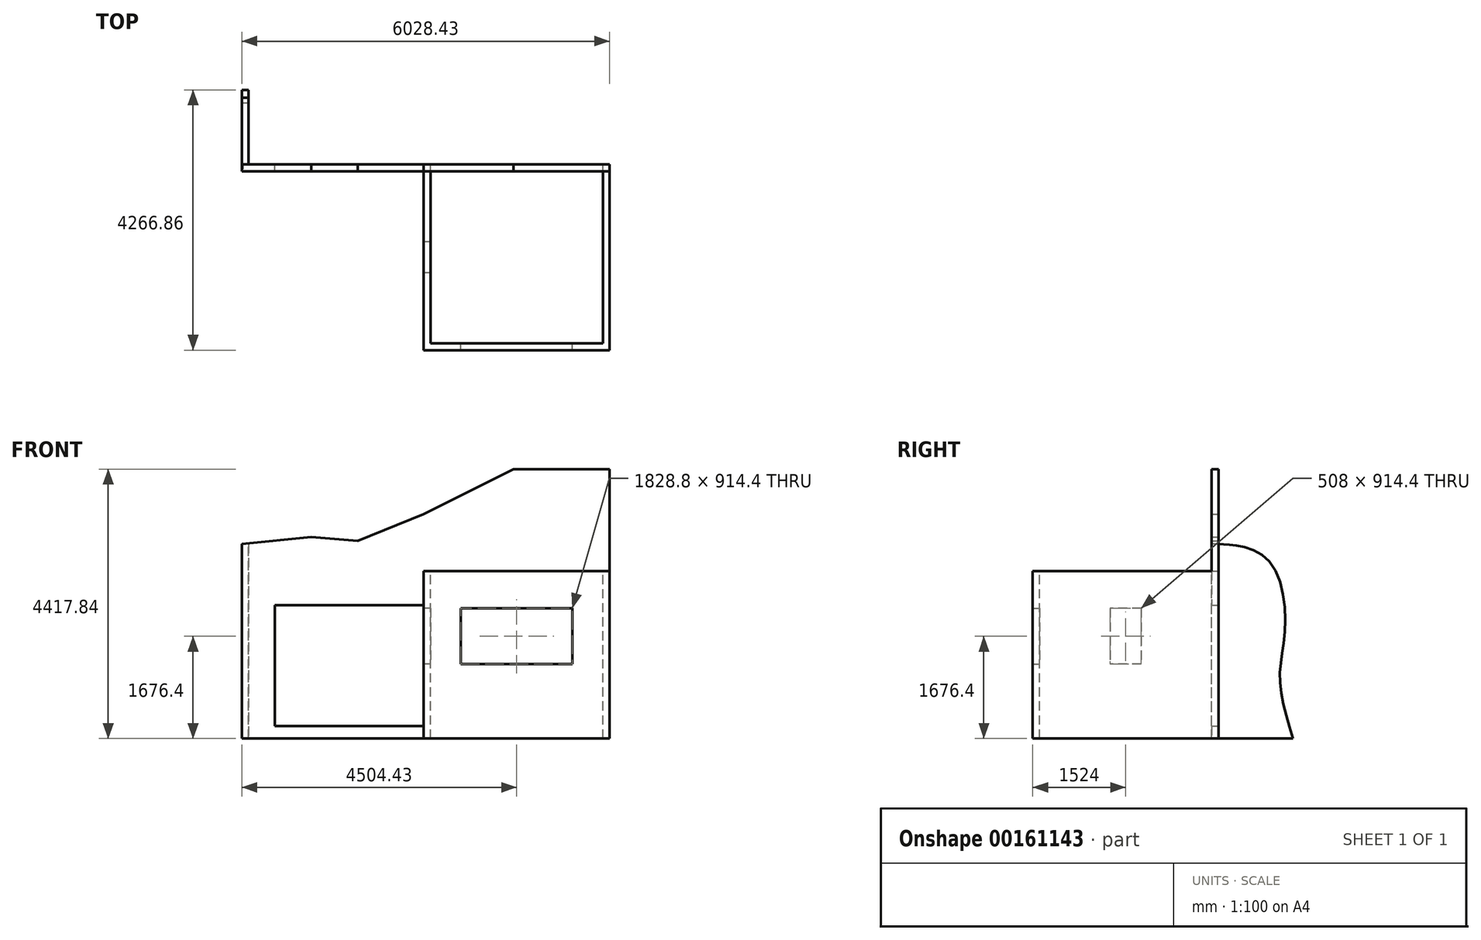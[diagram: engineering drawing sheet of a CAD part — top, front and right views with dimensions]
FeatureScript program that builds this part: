
annotation { "Feature Type Name" : "Feature", "Feature Type Description" : "" }
export const myFeature = defineFeature(function(context is Context, id is Id, definition is map)
    precondition{}
    {
        {
            var Q0;
            Q0=qCreatedBy(makeId("Front.planeOp"),FACE);
            var sketch = newSketch(context, id + "F0", { "sketchPlane" : qUnion([Q0])});
            skLineSegment(sketch, "E0.bottom", {"start": v(0, 0) * mm, "end": v(3048, 0) * mm});
            skLineSegment(sketch, "E0.top", {"start": v(0, 2743.2) * mm, "end": v(3048, 2743.2) * mm});
            skLineSegment(sketch, "E0.left", {"start": v(0, 0) * mm, "end": v(0, 2743.2) * mm});
            skLineSegment(sketch, "E0.right", {"start": v(3048, 0) * mm, "end": v(3048, 2743.2) * mm});
            skLineSegment(sketch, "E1.bottom", {"start": v(609.6, 2133.6) * mm, "end": v(2438.4, 2133.6) * mm});
            skLineSegment(sketch, "E1.top", {"start": v(609.6, 1219.2) * mm, "end": v(2438.4, 1219.2) * mm});
            skLineSegment(sketch, "E1.left", {"start": v(609.6, 2133.6) * mm, "end": v(609.6, 1219.2) * mm});
            skLineSegment(sketch, "E1.right", {"start": v(2438.4, 2133.6) * mm, "end": v(2438.4, 1219.2) * mm});
            skSolve(sketch);
        }
        {
            var Q0;
            Q0=qSketchRegion(id+"F0",true);
            extrude(context, id + "F1", {"entities" : qUnion([Q0]), "depth" : 114.04 * mm});
        }
        {
            var Q0;
            Q0=makeQuery(id+"F1.opExtrude","SWEPT_FACE",FACE,{"disambiguationData":[OSD([sQuery(id+"F0.wireOp",EDGE,"E0.left")])]});
            var sketch = newSketch(context, id + "F2", { "sketchPlane" : qUnion([Q0])});
            skLineSegment(sketch, "E2.bottom", {"start": v(114.04, 0) * mm, "end": v(-2933.96, 0) * mm});
            skLineSegment(sketch, "E2.top", {"start": v(114.04, 2743.2) * mm, "end": v(-2933.96, 2743.2) * mm});
            skLineSegment(sketch, "E2.left", {"start": v(114.04, 0) * mm, "end": v(114.04, 2743.2) * mm});
            skLineSegment(sketch, "E2.right", {"start": v(-2933.96, 0) * mm, "end": v(-2933.96, 2743.2) * mm});
            skLineSegment(sketch, "E3.bottom", {"start": v(-1663.96, 2133.6) * mm, "end": v(-1155.96, 2133.6) * mm});
            skLineSegment(sketch, "E3.top", {"start": v(-1663.96, 1219.2) * mm, "end": v(-1155.96, 1219.2) * mm});
            skLineSegment(sketch, "E3.left", {"start": v(-1663.96, 2133.6) * mm, "end": v(-1663.96, 1219.2) * mm});
            skLineSegment(sketch, "E3.right", {"start": v(-1155.96, 2133.6) * mm, "end": v(-1155.96, 1219.2) * mm});
            skSolve(sketch);
        }
        {
            var Q0;
            Q0=qSketchRegion(id+"F2",true);
            extrude(context, id + "F3", {"entities" : qUnion([Q0]), "operationType" : NewBodyOperationType.ADD, "oppositeDirection" : true, "depth" : 110 * mm});
        }
        {
            var Q0;
            Q0=makeQuery(id+"F1.opExtrude","SWEPT_FACE",FACE,{"disambiguationData":[OSD([sQuery(id+"F0.wireOp",EDGE,"E0.right")])]});
            var sketch = newSketch(context, id + "F4", { "sketchPlane" : qUnion([Q0])});
            skLineSegment(sketch, "E4.bottom", {"start": v(-114.04, 0) * mm, "end": v(2933.96, 0) * mm});
            skLineSegment(sketch, "E4.top", {"start": v(-114.04, 2743.2) * mm, "end": v(2933.96, 2743.2) * mm});
            skLineSegment(sketch, "E4.left", {"start": v(-114.04, 0) * mm, "end": v(-114.04, 2743.2) * mm});
            skLineSegment(sketch, "E4.right", {"start": v(2933.96, 0) * mm, "end": v(2933.96, 2743.2) * mm});
            skSolve(sketch);
        }
        {
            var Q0;
            Q0=qSketchRegion(id+"F4",true);
            extrude(context, id + "F5", {"entities" : qUnion([Q0]), "operationType" : NewBodyOperationType.ADD, "oppositeDirection" : true, "depth" : 110 * mm});
        }
        {
            var Q0;
            Q0=makeQuery(id+"F5.opExtrude","SWEPT_FACE",FACE,{"disambiguationData":[OSD([sQuery(id+"F4.wireOp",EDGE,"E4.right")])]});
            var sketch = newSketch(context, id + "F6", { "sketchPlane" : qUnion([Q0])});
            skLineSegment(sketch, "E5", {"start": v(-3048, 2743.2) * mm, "end": v(-67.57, 2743.2) * mm});
            skLineSegment(sketch, "E6", {"start": v(-67.57, 2743.2) * mm, "end": v(-67.57, 0) * mm});
            skLineSegment(sketch, "E7", {"start": v(-67.57, 0) * mm, "end": v(2980.43, 0) * mm});
            skLineSegment(sketch, "E8", {"start": v(2980.43, 0) * mm, "end": v(2980.43, 3189.02) * mm});
            skLineSegment(sketch, "E9", {"start": v(2980.43, 3189.02) * mm, "end": v(1845.9, 3306.68) * mm});
            skLineSegment(sketch, "E10", {"start": v(1845.9, 3306.68) * mm, "end": v(1081.13, 3239.45) * mm});
            skLineSegment(sketch, "E11", {"start": v(1081.13, 3239.45) * mm, "end": v(0, 3676.45) * mm});
            skLineSegment(sketch, "E12", {"start": v(0, 3676.45) * mm, "end": v(-1184.3, 4273.23) * mm});
            skLineSegment(sketch, "E13", {"start": v(-1184.3, 4273.23) * mm, "end": v(-1471.26, 4417.84) * mm});
            skLineSegment(sketch, "E14", {"start": v(-1471.26, 4417.84) * mm, "end": v(-3048, 4417.84) * mm});
            skLineSegment(sketch, "E15", {"start": v(-3048, 4417.84) * mm, "end": v(-3048, 2743.2) * mm});
            skSolve(sketch);
        }
        {
            var Q0;
            Q0=qSketchRegion(id+"F6",true);
            extrude(context, id + "F7", {"entities" : qUnion([Q0]), "operationType" : NewBodyOperationType.ADD, "oppositeDirection" : true, "depth" : 114.04 * mm});
        }
        {
            var Q0;
            Q0=makeQuery(id+"F7.boolean.opBoolean","MERGE",FACE,{"derivedFrom":[makeQuery(id+"F3.opExtrude","SWEPT_FACE",FACE,{"disambiguationData":[OSD([sQuery(id+"F2.wireOp",EDGE,"E2.right")])]}),makeQuery(id+"F5.opExtrude","SWEPT_FACE",FACE,{"disambiguationData":[OSD([sQuery(id+"F4.wireOp",EDGE,"E4.right")])]}),makeQuery(id+"F7.opExtrude","CAP_FACE",FACE,{"disambiguationData":[OSD([sQuery(id+"F6.wireOp",EDGE,"E5"),sQuery(id+"F6.wireOp",EDGE,"E6"),sQuery(id+"F6.wireOp",EDGE,"E7"),sQuery(id+"F6.wireOp",EDGE,"E8"),sQuery(id+"F6.wireOp",EDGE,"E9"),sQuery(id+"F6.wireOp",EDGE,"E10"),sQuery(id+"F6.wireOp",EDGE,"E11"),sQuery(id+"F6.wireOp",EDGE,"E12"),sQuery(id+"F6.wireOp",EDGE,"E13"),sQuery(id+"F6.wireOp",EDGE,"E14"),sQuery(id+"F6.wireOp",EDGE,"E15")])],"isStart":true})]});
            var sketch = newSketch(context, id + "F8", { "sketchPlane" : qUnion([Q0])});
            skLineSegment(sketch, "E16.bottom", {"start": v(0, 203.2) * mm, "end": v(2438.4, 203.2) * mm});
            skLineSegment(sketch, "E16.top", {"start": v(0, 2184.4) * mm, "end": v(2438.4, 2184.4) * mm});
            skLineSegment(sketch, "E16.left", {"start": v(0, 203.2) * mm, "end": v(0, 2184.4) * mm});
            skLineSegment(sketch, "E16.right", {"start": v(2438.4, 203.2) * mm, "end": v(2438.4, 2184.4) * mm});
            skSolve(sketch);
        }
        {
            var Q0;
            Q0=qSketchRegion(id+"F8",true);
            extrude(context, id + "F9", {"entities" : qUnion([Q0]), "oppositeDirection" : true, "depth" : 127 * mm});
        }
        {
            var Q0;
            Q0=makeQuery(id+"F9.opExtrude","SWEPT_BODY",BODY,{"disambiguationData":[OSD([sQuery(id+"F8.wireOp",EDGE,"E16.bottom"),sQuery(id+"F8.wireOp",EDGE,"E16.top"),sQuery(id+"F8.wireOp",EDGE,"E16.left"),sQuery(id+"F8.wireOp",EDGE,"E16.right")])]});
            var Q1;
            Q1=makeQuery(id+"F1.opExtrude","SWEPT_BODY",BODY,{"disambiguationData":[OSD([sQuery(id+"F0.wireOp",EDGE,"E0.bottom"),sQuery(id+"F0.wireOp",EDGE,"E0.top"),sQuery(id+"F0.wireOp",EDGE,"E0.left"),sQuery(id+"F0.wireOp",EDGE,"E0.right"),sQuery(id+"F0.wireOp",EDGE,"E1.bottom"),sQuery(id+"F0.wireOp",EDGE,"E1.top"),sQuery(id+"F0.wireOp",EDGE,"E1.left"),sQuery(id+"F0.wireOp",EDGE,"E1.right")])]});
            booleanBodies(context, id + "F10", {"operationType" : BooleanOperationType.SUBTRACTION, "tools" : qUnion([Q0]), "targets" : qUnion([Q1])});
        }
        {
            var Q0;
            Q0=makeQuery(id+"F7.opExtrude","SWEPT_FACE",FACE,{"disambiguationData":[OSD([sQuery(id+"F6.wireOp",EDGE,"E8")])]});
            var sketch = newSketch(context, id + "F11", { "sketchPlane" : qUnion([Q0])});
            skLineSegment(sketch, "E17", {"start": v(-2819.92, 0) * mm, "end": v(-4152.82, 0) * mm});
            skFitSpline(sketch, "E18", {"points": [v(-4152.82, 0) * mm, v(-3934.63, 987.92) * mm, v(-4021.9, 1795.21) * mm, v(-3767.35, 2900.69) * mm, v(-3185.52, 3169.79) * mm, v(-2933.96, 3189.02) * mm, v(-2819.92, 3189.02) * mm], "startDerivative": vector(1460.66, 4748.27) * mm, "endDerivative": vector(1460.56, -12.62) * mm});
            skLineSegment(sketch, "E19", {"start": v(-2819.92, 3189.02) * mm, "end": v(-2819.92, 0) * mm});
            skSolve(sketch);
        }
        {
            var Q0;
            Q0=qSketchRegion(id+"F11",true);
            extrude(context, id + "F12", {"entities" : qUnion([Q0]), "operationType" : NewBodyOperationType.ADD, "oppositeDirection" : true, "depth" : 110 * mm});
        }
    });
